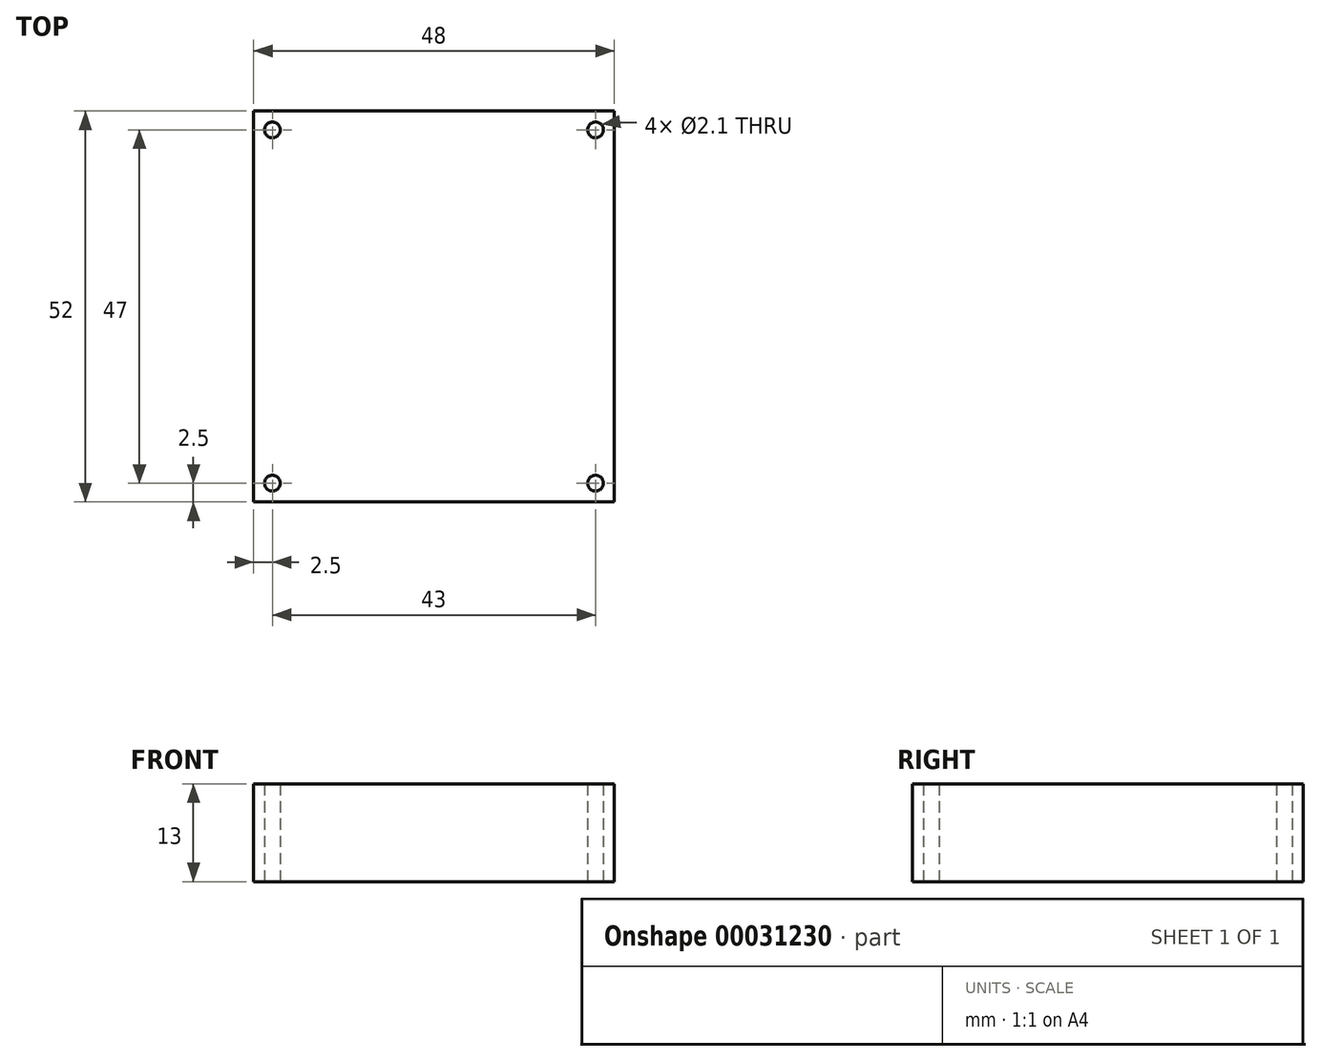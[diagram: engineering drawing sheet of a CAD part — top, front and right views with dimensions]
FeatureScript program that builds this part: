
annotation { "Feature Type Name" : "Feature", "Feature Type Description" : "" }
export const myFeature = defineFeature(function(context is Context, id is Id, definition is map)
    precondition{}
    {
        {
            var Q0;
            Q0=qCreatedBy(makeId("Top.planeOp"),FACE);
            var sketch = newSketch(context, id + "F0", { "sketchPlane" : qUnion([Q0])});
            skLineSegment(sketch, "E0.bottom", {"start": v(0, 0) * mm, "end": v(48, 0) * mm});
            skLineSegment(sketch, "E0.top", {"start": v(0, 52) * mm, "end": v(48, 52) * mm});
            skLineSegment(sketch, "E0.left", {"start": v(0, 0) * mm, "end": v(0, 52) * mm});
            skLineSegment(sketch, "E0.right", {"start": v(48, 0) * mm, "end": v(48, 52) * mm});
            skLineSegment(sketch, "E1", {"start": v(24, 52) * mm, "end": v(24, 0) * mm, "construction": true});
            skLineSegment(sketch, "E2", {"start": v(0, 26) * mm, "end": v(48, 26) * mm, "construction": true});
            skCircle(sketch, "E3", {"center": v(2.5, 49.5) * mm, "radius": 1.05 * mm});
            skCircle(sketch, "E4.MirrorC", {"center": v(45.5, 49.5) * mm, "radius": 1.05 * mm});
            skLineSegment(sketch, "E5.MirrorCS", {"start": v(48, 26) * mm, "end": v(0, 26) * mm, "construction": true});
            skCircle(sketch, "E6.MirrorC", {"center": v(2.5, 2.5) * mm, "radius": 1.05 * mm});
            skCircle(sketch, "E7.MirrorC", {"center": v(45.5, 2.5) * mm, "radius": 1.05 * mm});
            skSolve(sketch);
        }
        {
            var Q0;
            Q0 = qSketchRegion(id + "F0", true);
            extrude(context, id + "F1", {"entities" : qUnion([Q0]), "depth" : 13 * mm});
        }
    });
